# Revit family: Drain_Offset_Open-Grid_Commercial_American-Standard_7723018.002
name_source: partatom
category: Plumbing Fixtures
units: mm (PartAtom-declared; Revit-internal decimal feet)

## family parameters
Always vertical = No
Cut with Voids When Loaded = No
OmniClass Number = 23.45.05.14.99
OmniClass Title = Other Sanitary Washing Plumbing Fixtures
Part Type = Normal
Room Calculation Point = No
Round Connector Dimension = Use Diameter
Shared = Yes
Work Plane-Based = Yes

## types (1)
- 7723018.002
    A = 3"
    ADA Compliant = Yes
    Assembly Code = D2030400
    CW Connection = No
    CWFU = 3
    Default Elevation = 0"
    Description = Offset grid drain with overflow for wheelchair lavatory. 4-3/4" to 5" offset. Brass construction.
    Finish = Brass-American Standard-002-Polished Chrome
    HW Connection = No
    HWFU = 3
    IAPMO Compliance = ASME A112.18.2, CSA B 125.2
    Installation Type = Surface Mounted
    Manufacturer = American Standard
    Material = Brass-American Standard-002-Polished Chrome
    Min Max Adjustable Length = 1 1/2"
    Model = 7723018.002
    Price = Prices may vary. Please consult Manufacturer Representative for most up-to-date price list.
    Product Documentation Link = https://lixil.cdn.celum.cloud
    Product Page URL = https://www.americanstandard.ca
    Revised Date = 09/25/2024
    URL = https://www.americanstandard.ca
    Vent Connection = No
    WFU = 4
    Waste Connection = Yes
    Width = 2 3/16"

## geometry (parser evidence)
native form markers: Sweep x2
no freeform markers — native parametric forms only
